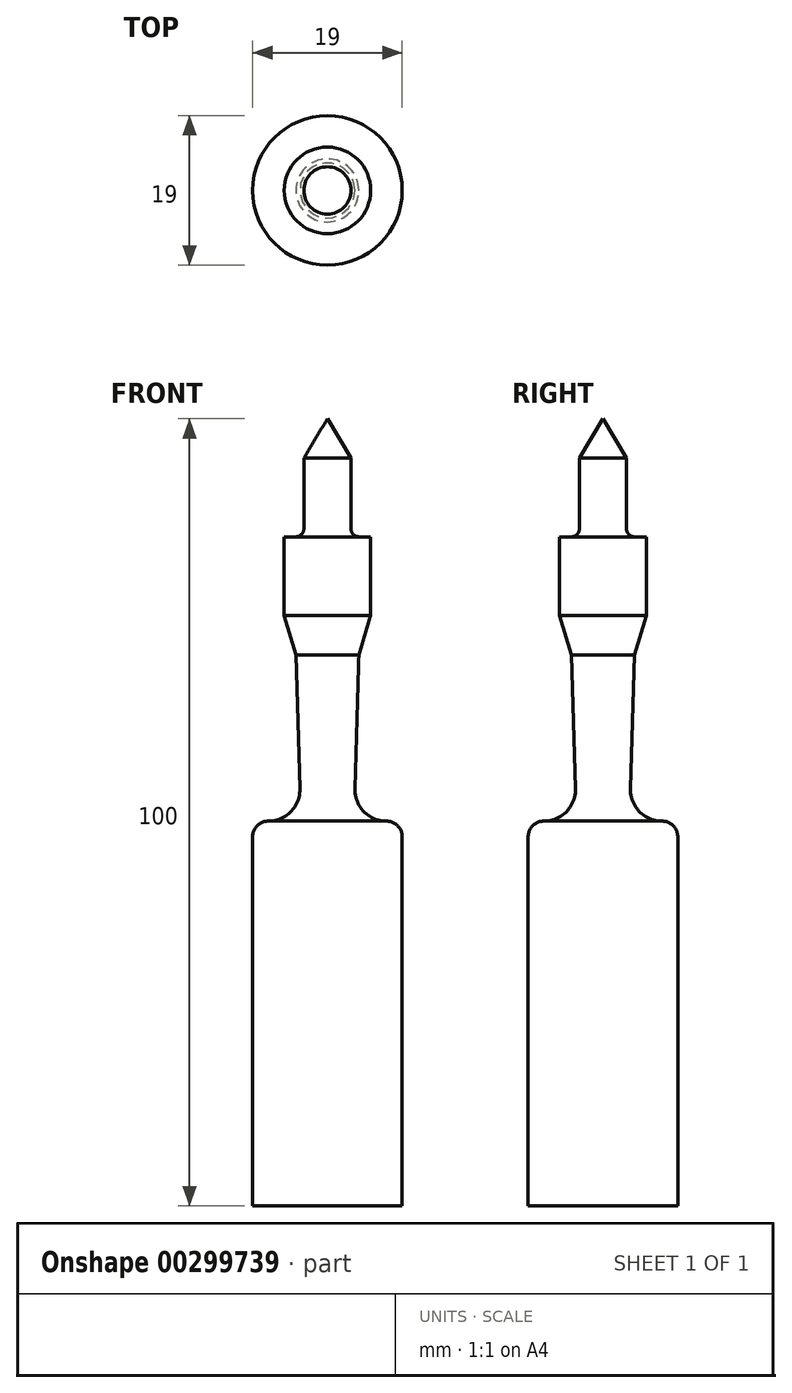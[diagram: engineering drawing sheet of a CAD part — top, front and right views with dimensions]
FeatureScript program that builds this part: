
annotation { "Feature Type Name" : "Feature", "Feature Type Description" : "" }
export const myFeature = defineFeature(function(context is Context, id is Id, definition is map)
    precondition{}
    {
        {
            var Q0;
            Q0=qCreatedBy(makeId("Front.planeOp"),FACE);
            var sketch = newSketch(context, id + "F0", { "sketchPlane" : qUnion([Q0])});
            skLineSegment(sketch, "E0", {"start": v(0, 0) * mm, "end": v(0, -100) * mm});
            skLineSegment(sketch, "E1", {"start": v(0, 0) * mm, "end": v(3, -5) * mm});
            skLineSegment(sketch, "E2", {"start": v(3, -5) * mm, "end": v(3, -14) * mm});
            skArc(sketch, "E3", {"start": v(3, -14) * mm, "mid": v(3.3, -14.7) * mm, "end": v(4, -15) * mm});
            skLineSegment(sketch, "E4", {"start": v(4, -15) * mm, "end": v(5.5, -15) * mm});
            skLineSegment(sketch, "E5", {"start": v(5.5, -15) * mm, "end": v(5.5, -25) * mm});
            skLineSegment(sketch, "E6", {"start": v(5.5, -25) * mm, "end": v(4, -30) * mm});
            skLineSegment(sketch, "E7", {"start": v(4, -30) * mm, "end": v(3.5, -47) * mm});
            skArc(sketch, "E8", {"start": v(3.5, -47) * mm, "mid": v(4.63, -49.9) * mm, "end": v(7.5, -51.12) * mm});
            skArc(sketch, "E9", {"start": v(9.5, -53.12) * mm, "mid": v(8.91, -51.7) * mm, "end": v(7.5, -51.12) * mm});
            skLineSegment(sketch, "E10", {"start": v(9.5, -53.12) * mm, "end": v(9.5, -100) * mm});
            skLineSegment(sketch, "E11", {"start": v(9.5, -100) * mm, "end": v(0, -100) * mm});
            skSolve(sketch);
        }
        {
            var Q0;
            Q0=makeQuery(id+"F0.imprint","IMPRINT",FACE,{"disambiguationData":[TD([[makeQuery(id+"F0.imprint","IMPRINT",EDGE,{"derivedFrom":sQuery(id+"F0.wireOp",EDGE,"E0")}),1.0]])]});
            var Q1;
            Q1=sQuery(id+"F0.wireOp",EDGE,"E0");
            revolve(context, id + "F1", {"entities" : qUnion([Q0]), "axis" : qUnion([Q1]), "revolveType" : RevolveType.FULL});
        }
    });
